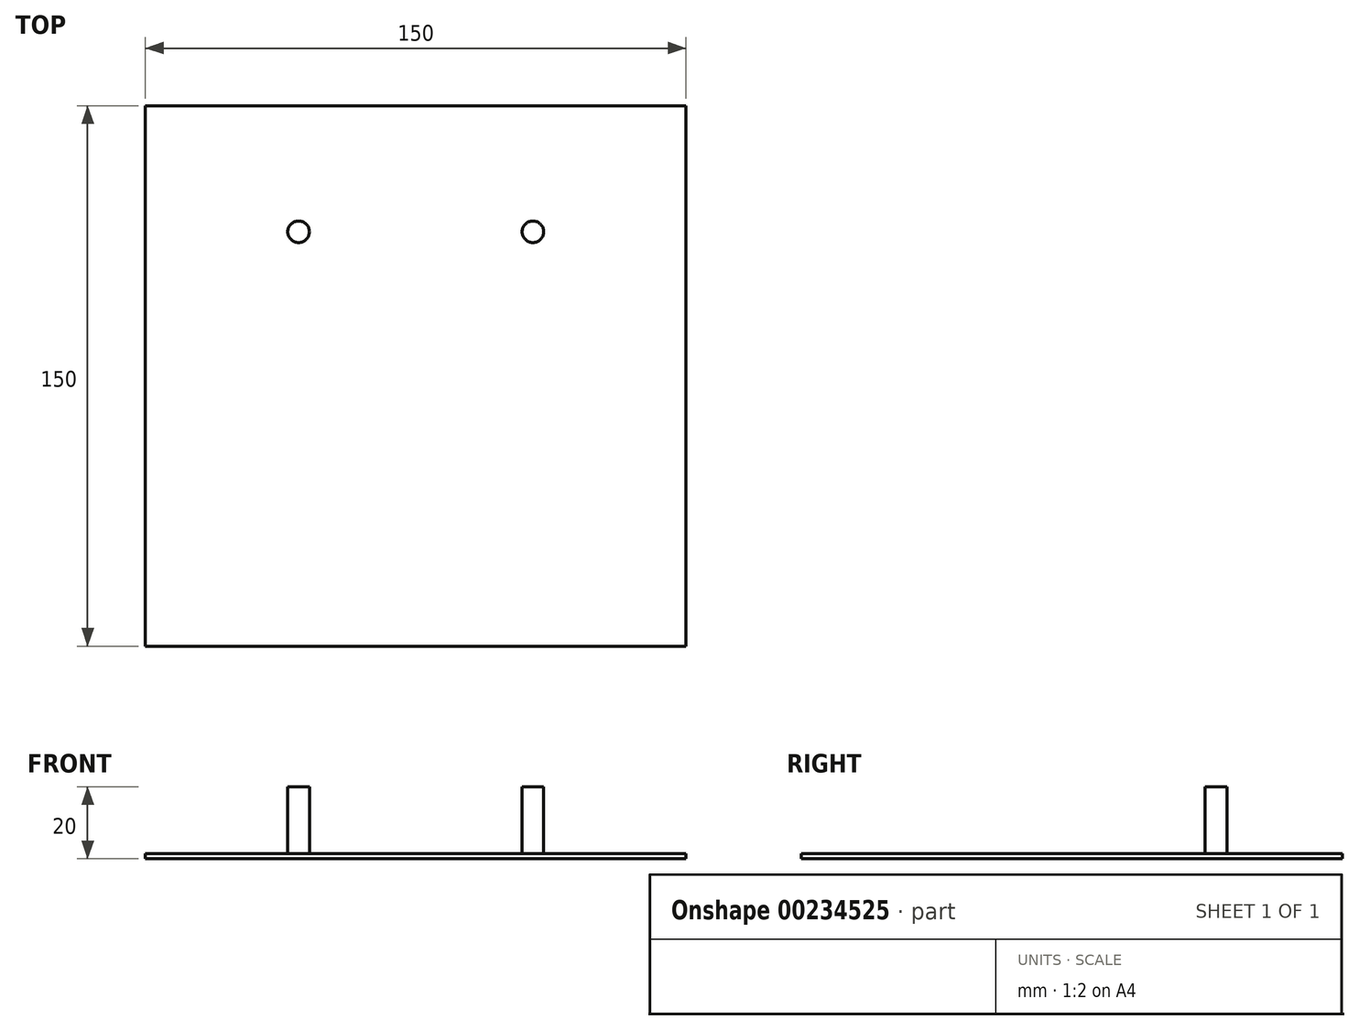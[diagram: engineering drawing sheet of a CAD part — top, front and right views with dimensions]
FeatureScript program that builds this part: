
annotation { "Feature Type Name" : "Feature", "Feature Type Description" : "" }
export const myFeature = defineFeature(function(context is Context, id is Id, definition is map)
    precondition{}
    {
        {
            var Q0;
            Q0=qCreatedBy(makeId("Top.planeOp"),FACE);
            var sketch = newSketch(context, id + "F0", { "sketchPlane" : qUnion([Q0])});
            skLineSegment(sketch, "E0.bottom", {"start": v(-83.75, 105.28) * mm, "end": v(66.25, 105.28) * mm});
            skLineSegment(sketch, "E0.top", {"start": v(-83.75, -44.72) * mm, "end": v(66.25, -44.72) * mm});
            skLineSegment(sketch, "E0.left", {"start": v(-83.75, 105.28) * mm, "end": v(-83.75, -44.72) * mm});
            skLineSegment(sketch, "E0.right", {"start": v(66.25, 105.28) * mm, "end": v(66.25, -44.72) * mm});
            skLineSegment(sketch, "E1", {"start": v(-83.75, 70.28) * mm, "end": v(-44.25, 70.28) * mm, "construction": true});
            skLineSegment(sketch, "E2", {"start": v(-8.75, 105.28) * mm, "end": v(-8.75, -44.72) * mm, "construction": true});
            skLineSegment(sketch, "E3", {"start": v(-41.25, 105.28) * mm, "end": v(-41.25, 73.28) * mm, "construction": true});
            skLineSegment(sketch, "E4", {"start": v(23.75, 105.28) * mm, "end": v(23.75, 73.28) * mm, "construction": true});
            skCircle(sketch, "E5", {"center": v(-41.25, 70.28) * mm, "radius": 3 * mm});
            skCircle(sketch, "E6", {"center": v(23.75, 70.28) * mm, "radius": 3 * mm});
            skLineSegment(sketch, "E7.trimOffspring", {"start": v(-38.25, 70.28) * mm, "end": v(20.75, 70.28) * mm, "construction": true});
            skLineSegment(sketch, "E8.trimOffspring", {"start": v(-41.25, 67.28) * mm, "end": v(-41.25, -44.72) * mm, "construction": true});
            skLineSegment(sketch, "E9.trimOffspring", {"start": v(23.75, 67.28) * mm, "end": v(23.75, -44.72) * mm, "construction": true});
            skLineSegment(sketch, "E10.trimOffspring", {"start": v(26.75, 70.28) * mm, "end": v(66.25, 70.28) * mm, "construction": true});
            skSolve(sketch);
        }
        {
            var Q0;
            Q0 = qSketchRegion(id + "F0", true);
            extrude(context, id + "F1", {"entities" : qUnion([Q0]), "depth" : 1.5 * mm});
        }
        {
            var Q0;
            Q0=makeQuery(id+"F0.imprint","IMPRINT",FACE,{"disambiguationData":[TD([[makeQuery(id+"F0.imprint","IMPRINT",EDGE,{"derivedFrom":sQuery(id+"F0.wireOp",EDGE,"E5")}),1.0]])]});
            var Q1;
            Q1=makeQuery(id+"F0.imprint","IMPRINT",FACE,{"disambiguationData":[TD([[makeQuery(id+"F0.imprint","IMPRINT",EDGE,{"derivedFrom":sQuery(id+"F0.wireOp",EDGE,"E6")}),1.0]])]});
            extrude(context, id + "F2", {"entities" : qUnion([Q0, Q1]), "operationType" : NewBodyOperationType.ADD, "depth" : 20 * mm});
        }
    });
